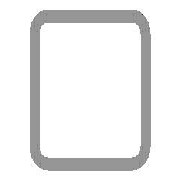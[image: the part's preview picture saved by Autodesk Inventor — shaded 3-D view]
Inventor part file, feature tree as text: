
AUTODESK INVENTOR PART (.ipt)
format: ipt  version: 2024.2 (Build 282272000, 272)  size: 129,536 bytes
history: native  units: mm (DEFAULTED — no unit token found)
features: other x4, sketch x1, plane x1
ambient origin geometry x8: Origin, YZ Plane, XZ Plane, XY Plane, X Axis, Y Axis, Z Axis, Center Point
bodies: Solid1 (feature_tree), Body (feature_tree)
feature tree (6):
  parser-record x1  (decoder bookkeeping rows leaked as tree rows — omitted from the tree; the rows remain in map.json)
  other  "Driven Length"
  other  "Start Plane"
  other  "End Plane"
  sketch  "Sketch3"  dims[d3=540.0mm d4=0.0mm d7=6.0mm d9=50.0mm d11=50.0mm d12=3.0mm d13=20.0mm d14=560.0mm d15=25.0mm d16=25.0mm d17=90.0deg d18=540.0mm]
  plane  "Work Plane3"
